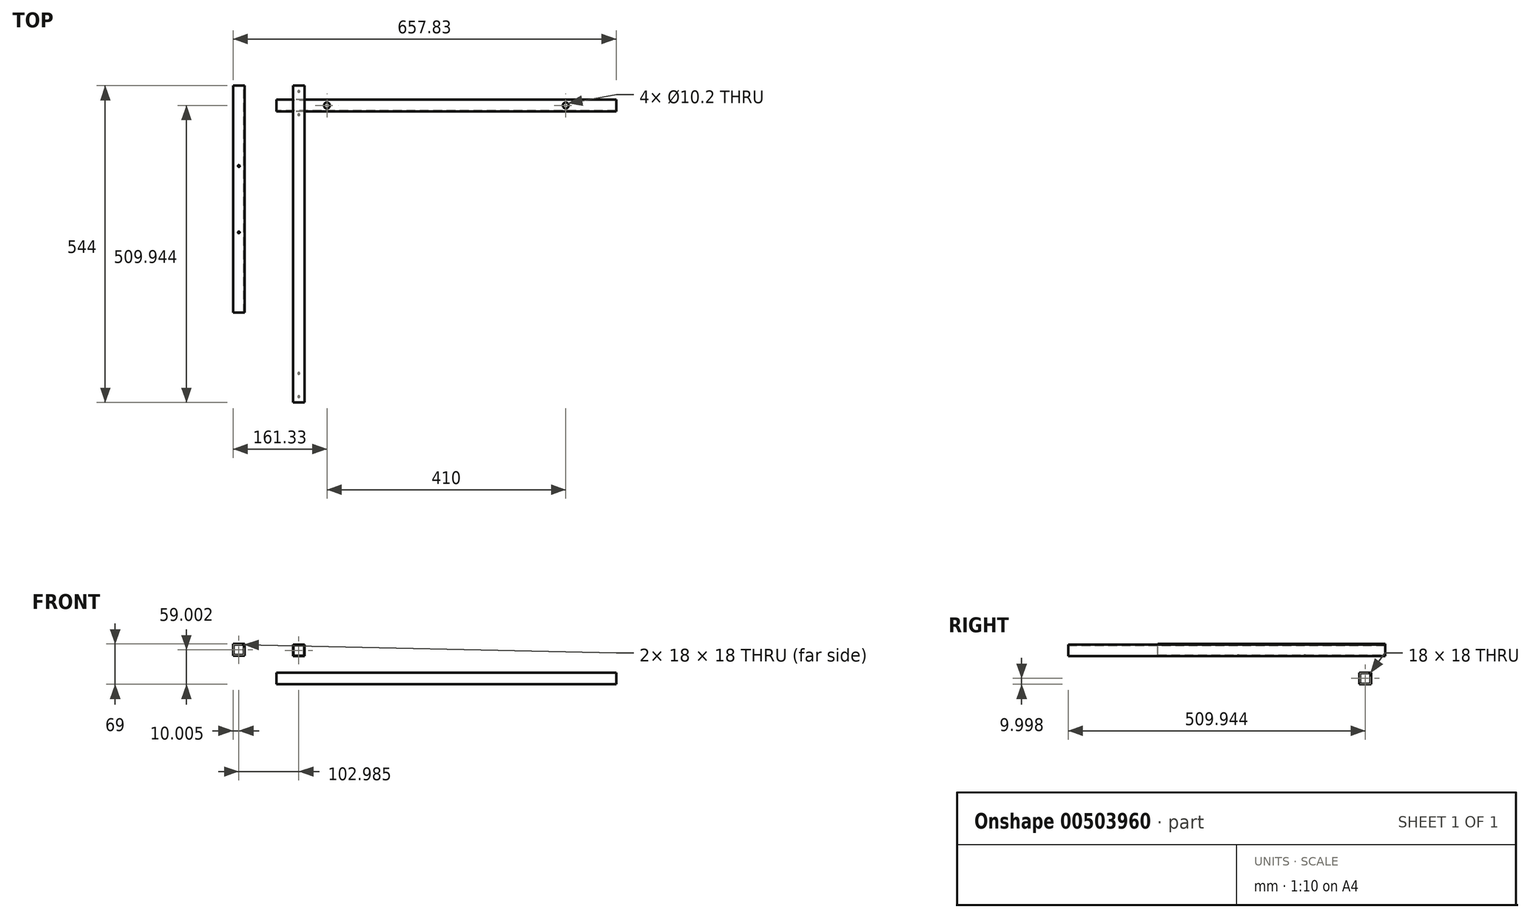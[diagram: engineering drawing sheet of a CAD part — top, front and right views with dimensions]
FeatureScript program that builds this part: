
annotation { "Feature Type Name" : "Feature", "Feature Type Description" : "" }
export const myFeature = defineFeature(function(context is Context, id is Id, definition is map)
    precondition{}
    {
        {
            var Q0;
            Q0=qCreatedBy(makeId("Front.planeOp"),FACE);
            var sketch = newSketch(context, id + "F0", { "sketchPlane" : qUnion([Q0])});
            skLineSegment(sketch, "E0.bottom", {"start": v(-54.83, 30.61) * mm, "end": v(-74.83, 30.61) * mm});
            skLineSegment(sketch, "E0.top", {"start": v(-54.83, 50.61) * mm, "end": v(-74.83, 50.61) * mm});
            skLineSegment(sketch, "E0.left", {"start": v(-54.83, 30.61) * mm, "end": v(-54.83, 50.61) * mm});
            skLineSegment(sketch, "E0.right", {"start": v(-74.83, 30.61) * mm, "end": v(-74.83, 50.61) * mm});
            skPoint(sketch, "E0.middle", {"position": v(-64.83, 40.61) * mm});
            skLineSegment(sketch, "E1.bottom", {"start": v(-55.83, 31.61) * mm, "end": v(-73.83, 31.61) * mm});
            skLineSegment(sketch, "E1.top", {"start": v(-55.83, 49.61) * mm, "end": v(-73.83, 49.61) * mm});
            skLineSegment(sketch, "E1.left", {"start": v(-55.83, 31.61) * mm, "end": v(-55.83, 49.61) * mm});
            skLineSegment(sketch, "E1.right", {"start": v(-73.83, 31.61) * mm, "end": v(-73.83, 49.61) * mm});
            skSolve(sketch);
        }
        {
            var Q0;
            Q0=makeQuery(id+"F0.imprint","IMPRINT",FACE,{"disambiguationData":[TD([[makeQuery(id+"F0.imprint","IMPRINT",EDGE,{"derivedFrom":sQuery(id+"F0.wireOp",EDGE,"E0.bottom")}),-1.0]])]});
            extrude(context, id + "F1", {"entities" : qUnion([Q0]), "depth" : 390 * mm, "offsetDistance" : 25 * mm});
        }
        {
            var Q0;
            Q0=makeQuery(id+"F1.opExtrude","SWEPT_FACE",FACE,{"disambiguationData":[OSD([sQuery(id+"F0.wireOp",EDGE,"E0.top")])]});
            var sketch = newSketch(context, id + "F2", { "sketchPlane" : qUnion([Q0])});
            skLineSegment(sketch, "E2", {"start": v(-74.83, -195) * mm, "end": v(-54.83, -195) * mm, "construction": true});
            skLineSegment(sketch, "E3", {"start": v(-64.83, 0) * mm, "end": v(-64.83, -390) * mm, "construction": true});
            skCircle(sketch, "E4", {"center": v(-64.83, -138) * mm, "radius": 1.55 * mm});
            skCircle(sketch, "E5", {"center": v(-64.83, -252) * mm, "radius": 1.55 * mm});
            skSolve(sketch);
        }
        {
            var Q0;
            Q0=makeQuery(id+"F2.imprint","IMPRINT",FACE,{"disambiguationData":[TD([[makeQuery(id+"F2.imprint","IMPRINT",EDGE,{"derivedFrom":sQuery(id+"F2.wireOp",EDGE,"E4")}),1.0]])]});
            var Q1;
            Q1=makeQuery(id+"F2.imprint","IMPRINT",FACE,{"disambiguationData":[TD([[makeQuery(id+"F2.imprint","IMPRINT",EDGE,{"derivedFrom":sQuery(id+"F2.wireOp",EDGE,"E5")}),1.0]])]});
            var Q2;
            Q2=makeQuery(id+"F2.imprint","IMPRINT",FACE,{"disambiguationData":[TD([[makeQuery(id+"F2.imprint","IMPRINT",EDGE,{"derivedFrom":sQuery(id+"F2.wireOp",EDGE,"VpgW0fwV-EMno-4I85-Xoet-6qAiJqKx4oq7")}),1.0]])]});
            var Q3;
            Q3=makeQuery(id+"F2.imprint","IMPRINT",FACE,{"disambiguationData":[TD([[makeQuery(id+"F2.imprint","IMPRINT",EDGE,{"derivedFrom":sQuery(id+"F2.wireOp",EDGE,"N5m8n6pL-D1Kh-QstU-woXE-ZA8hCv9KQPBE")}),1.0]])]});
            var Q4;
            Q4=makeQuery(id+"F1.opExtrude","SWEPT_FACE",FACE,{"disambiguationData":[OSD([sQuery(id+"F0.wireOp",EDGE,"E0.bottom")])]});
            extrude(context, id + "F3", {"entities" : qUnion([Q0, Q1, Q2, Q3]), "operationType" : NewBodyOperationType.REMOVE, "endBound" : BoundingType.UP_TO_SURFACE, "oppositeDirection" : true, "depth" : 25 * mm, "endBoundEntityFace" : qUnion([Q4]), "offsetDistance" : 25 * mm});
        }
        {
            var Q0;
            Q0=qCreatedBy(makeId("Right.planeOp"),FACE);
            var sketch = newSketch(context, id + "F4", { "sketchPlane" : qUnion([Q0])});
            skLineSegment(sketch, "E6.bottom", {"start": v(-24.06, -18.4) * mm, "end": v(-44.06, -18.4) * mm});
            skLineSegment(sketch, "E6.top", {"start": v(-24.06, 1.6) * mm, "end": v(-44.06, 1.6) * mm});
            skLineSegment(sketch, "E6.left", {"start": v(-24.06, -18.4) * mm, "end": v(-24.06, 1.6) * mm});
            skLineSegment(sketch, "E6.right", {"start": v(-44.06, -18.4) * mm, "end": v(-44.06, 1.6) * mm});
            skPoint(sketch, "E6.middle", {"position": v(-34.06, -8.4) * mm});
            skLineSegment(sketch, "E7.bottom", {"start": v(-25.06, -17.4) * mm, "end": v(-43.06, -17.4) * mm});
            skLineSegment(sketch, "E7.top", {"start": v(-25.06, 0.6) * mm, "end": v(-43.06, 0.6) * mm});
            skLineSegment(sketch, "E7.left", {"start": v(-25.06, -17.4) * mm, "end": v(-25.06, 0.6) * mm});
            skLineSegment(sketch, "E7.right", {"start": v(-43.06, -17.4) * mm, "end": v(-43.06, 0.6) * mm});
            skSolve(sketch);
        }
        {
            var Q0;
            Q0=makeQuery(id+"F4.imprint","IMPRINT",FACE,{"disambiguationData":[TD([[makeQuery(id+"F4.imprint","IMPRINT",EDGE,{"derivedFrom":sQuery(id+"F4.wireOp",EDGE,"E6.bottom")}),-1.0]])]});
            extrude(context, id + "F5", {"entities" : qUnion([Q0]), "depth" : 583 * mm, "offsetDistance" : 25 * mm});
        }
        {
            var Q0;
            Q0=makeQuery(id+"F5.opExtrude","SWEPT_FACE",FACE,{"disambiguationData":[OSD([sQuery(id+"F4.wireOp",EDGE,"E6.top")])]});
            var sketch = newSketch(context, id + "F6", { "sketchPlane" : qUnion([Q0])});
            skLineSegment(sketch, "E8", {"start": v(0, -34.06) * mm, "end": v(583, -34.06) * mm, "construction": true});
            skLineSegment(sketch, "E9", {"start": v(291.5, -24.06) * mm, "end": v(291.5, -44.06) * mm, "construction": true});
            skCircle(sketch, "E10", {"center": v(86.5, -34.06) * mm, "radius": 5.1 * mm});
            skCircle(sketch, "E11", {"center": v(496.5, -34.06) * mm, "radius": 5.1 * mm});
            skSolve(sketch);
        }
        {
            var Q0;
            Q0=makeQuery(id+"F6.imprint","IMPRINT",FACE,{"disambiguationData":[TD([[makeQuery(id+"F6.imprint","IMPRINT",EDGE,{"derivedFrom":sQuery(id+"F6.wireOp",EDGE,"E10")}),1.0]])]});
            var Q1;
            Q1=makeQuery(id+"F6.imprint","IMPRINT",FACE,{"disambiguationData":[TD([[makeQuery(id+"F6.imprint","IMPRINT",EDGE,{"derivedFrom":sQuery(id+"F6.wireOp",EDGE,"E11")}),1.0]])]});
            var Q2;
            Q2=makeQuery(id+"F6.imprint","IMPRINT",FACE,{"disambiguationData":[TD([[makeQuery(id+"F6.imprint","IMPRINT",EDGE,{"derivedFrom":sQuery(id+"F6.wireOp",EDGE,"PCmSx0hz-Ih9Z-UxrI-Vqkk-CvFnhpPuiLUB")}),1.0]])]});
            var Q3;
            Q3=makeQuery(id+"F6.imprint","IMPRINT",FACE,{"disambiguationData":[TD([[makeQuery(id+"F6.imprint","IMPRINT",EDGE,{"derivedFrom":sQuery(id+"F6.wireOp",EDGE,"bp3JQaYy-BQyk-Obnn-yjsj-c2vtYo4bC5bP")}),1.0]])]});
            extrude(context, id + "F7", {"entities" : qUnion([Q0, Q1, Q2, Q3]), "operationType" : NewBodyOperationType.REMOVE, "endBound" : BoundingType.THROUGH_ALL, "oppositeDirection" : true, "depth" : 25 * mm, "offsetDistance" : 25 * mm});
        }
        {
            var Q0;
            Q0=qCreatedBy(makeId("Front.planeOp"),FACE);
            var sketch = newSketch(context, id + "F8", { "sketchPlane" : qUnion([Q0])});
            skLineSegment(sketch, "E12.bottom", {"start": v(48.16, 29.68) * mm, "end": v(28.16, 29.68) * mm});
            skLineSegment(sketch, "E12.top", {"start": v(48.16, 49.68) * mm, "end": v(28.16, 49.68) * mm});
            skLineSegment(sketch, "E12.left", {"start": v(48.16, 29.68) * mm, "end": v(48.16, 49.68) * mm});
            skLineSegment(sketch, "E12.right", {"start": v(28.16, 29.68) * mm, "end": v(28.16, 49.68) * mm});
            skPoint(sketch, "E12.middle", {"position": v(38.16, 39.68) * mm});
            skLineSegment(sketch, "E13.bottom", {"start": v(47.16, 30.68) * mm, "end": v(29.16, 30.68) * mm});
            skLineSegment(sketch, "E13.top", {"start": v(47.16, 48.68) * mm, "end": v(29.16, 48.68) * mm});
            skLineSegment(sketch, "E13.left", {"start": v(47.16, 30.68) * mm, "end": v(47.16, 48.68) * mm});
            skLineSegment(sketch, "E13.right", {"start": v(29.16, 30.68) * mm, "end": v(29.16, 48.68) * mm});
            skSolve(sketch);
        }
        {
            var Q0;
            Q0=makeQuery(id+"F8.imprint","IMPRINT",FACE,{"disambiguationData":[TD([[makeQuery(id+"F8.imprint","IMPRINT",EDGE,{"derivedFrom":sQuery(id+"F8.wireOp",EDGE,"E12.bottom")}),-1.0]])]});
            extrude(context, id + "F9", {"entities" : qUnion([Q0]), "depth" : 544 * mm, "offsetDistance" : 25 * mm});
        }
        {
            var Q0;
            Q0=makeQuery(id+"F9.opExtrude","SWEPT_FACE",FACE,{"disambiguationData":[OSD([sQuery(id+"F8.wireOp",EDGE,"E12.bottom")])]});
            var sketch = newSketch(context, id + "F10", { "sketchPlane" : qUnion([Q0])});
            skLineSegment(sketch, "E14", {"start": v(38.16, 544) * mm, "end": v(38.16, 0) * mm, "construction": true});
            skLineSegment(sketch, "E15", {"start": v(28.16, 272) * mm, "end": v(48.16, 272) * mm, "construction": true});
            skCircle(sketch, "E16", {"center": v(38.16, 534) * mm, "radius": 1.6 * mm});
            skCircle(sketch, "E17", {"center": v(38.16, 494) * mm, "radius": 1.6 * mm});
            skCircle(sketch, "E18", {"center": v(38.16, 50) * mm, "radius": 1.6 * mm});
            skCircle(sketch, "E19", {"center": v(38.16, 10) * mm, "radius": 1.6 * mm});
            skSolve(sketch);
        }
        {
            var Q0;
            Q0=makeQuery(id+"F10.imprint","IMPRINT",FACE,{"disambiguationData":[TD([[makeQuery(id+"F10.imprint","IMPRINT",EDGE,{"derivedFrom":sQuery(id+"F10.wireOp",EDGE,"E19")}),1.0]])]});
            var Q1;
            Q1=makeQuery(id+"F10.imprint","IMPRINT",FACE,{"disambiguationData":[TD([[makeQuery(id+"F10.imprint","IMPRINT",EDGE,{"derivedFrom":sQuery(id+"F10.wireOp",EDGE,"E18")}),1.0]])]});
            var Q2;
            Q2=makeQuery(id+"F10.imprint","IMPRINT",FACE,{"disambiguationData":[TD([[makeQuery(id+"F10.imprint","IMPRINT",EDGE,{"derivedFrom":sQuery(id+"F10.wireOp",EDGE,"E17")}),1.0]])]});
            var Q3;
            Q3=makeQuery(id+"F10.imprint","IMPRINT",FACE,{"disambiguationData":[TD([[makeQuery(id+"F10.imprint","IMPRINT",EDGE,{"derivedFrom":sQuery(id+"F10.wireOp",EDGE,"E16")}),1.0]])]});
            extrude(context, id + "F11", {"entities" : qUnion([Q0, Q1, Q2, Q3]), "operationType" : NewBodyOperationType.REMOVE, "endBound" : BoundingType.UP_TO_NEXT, "oppositeDirection" : true, "depth" : 25 * mm, "offsetDistance" : 25 * mm});
        }
    });
